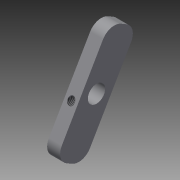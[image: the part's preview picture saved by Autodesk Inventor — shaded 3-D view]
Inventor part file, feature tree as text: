
AUTODESK INVENTOR PART (.ipt)
format: ipt  version: 2015 (Build 190159000, 159)  size: 123,904 bytes
history: native  units: mm
features: hole x3, sketch x3, extrude x1, fillet x1, projected_geometry x1
ambient origin geometry x8: Origin, YZ Plane, XZ Plane, XY Plane, X Axis, Y Axis, Z Axis, Center Point
bodies: Solid1 (feature_tree)
feature tree (9):
  extrude  "Extrusion1"  Depth=50.0mm
  hole  "Hole1"  [1 undecoded]
  hole  "Hole2"  [1 undecoded]
  hole  "Hole3"  [1 undecoded]
  fillet  "Fillet1"  Radius=6.0mm
  sketch  "Sketch2"  dims[d1=15.0mm d2=50.0mm]
  sketch  "Sketch3"  dims[d4=60.0deg d5=6.0mm d6=0.0mm]
  sketch  "Sketch4"  dims[d7=8.0mm d8=6.0mm d9=4.0mm d10=2.0mm d11=90.0deg d12=8.0mm d13=20.594885mm d14=3.242mm d15=8.0mm d16=4.0mm d17=2.0mm d18=90.0deg d19=11.8mm d20=20.594885mm d21=20.0mm d22=20.0mm d23=3.459mm d24=8.0mm d25=4.0mm d26=2.0mm d27=90.0deg d28=4.0mm d29=20.594885mm d30=6.0mm d31=1.0mm d32=1.0mm]
  projected_geometry  "Projected Loop1"
note: 3 required parameter values undecoded (feature->parameter linkage not recoverable at this tier; creation-order binding heuristic only, values carry confidence <= 0.55)
